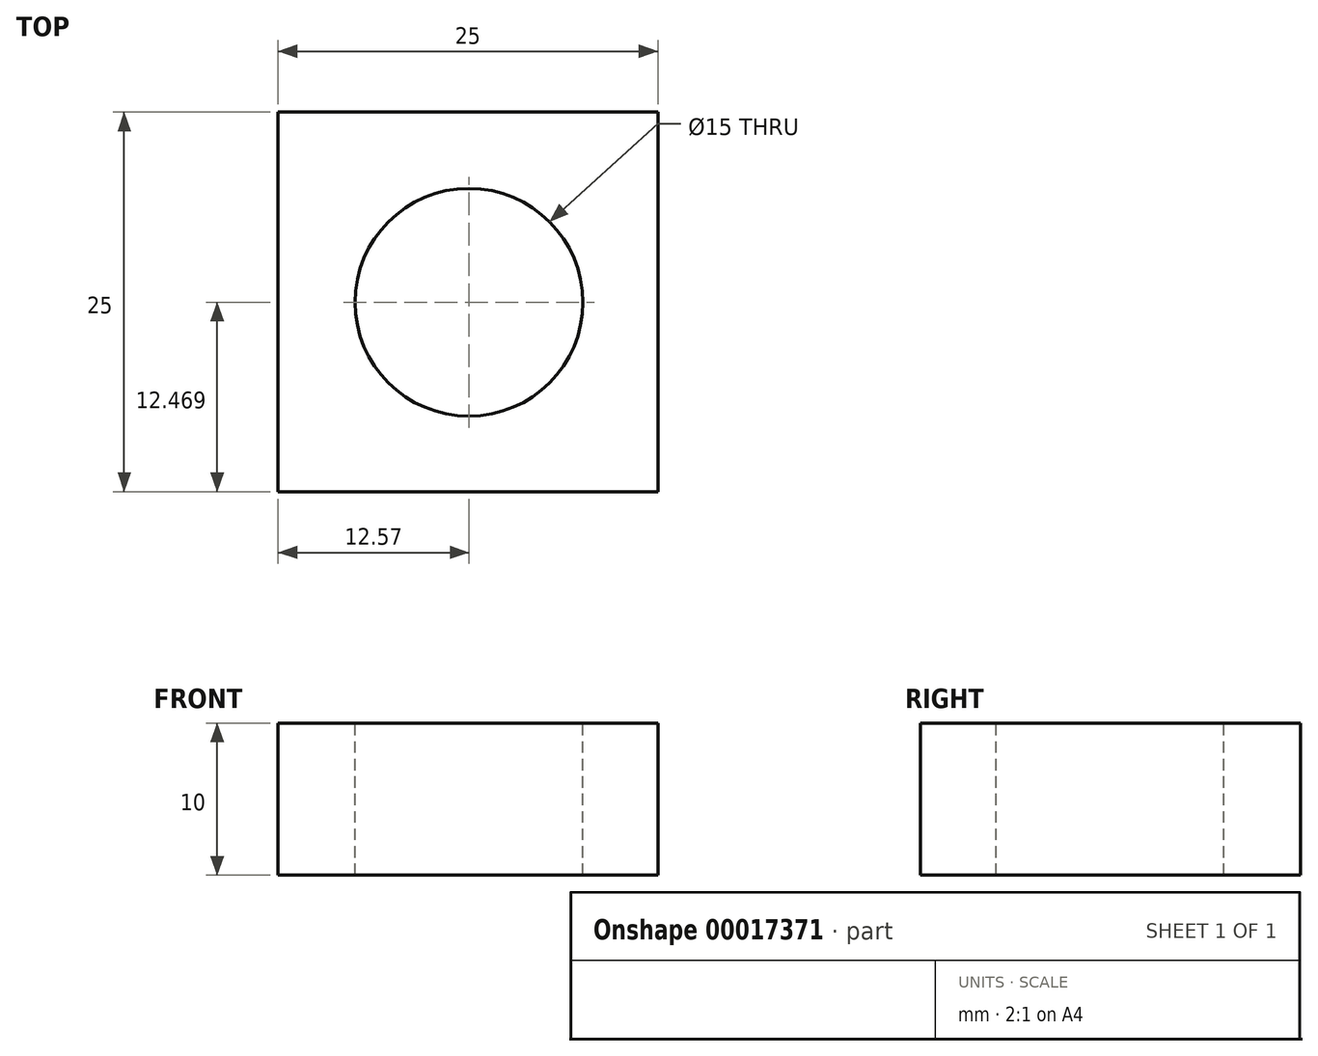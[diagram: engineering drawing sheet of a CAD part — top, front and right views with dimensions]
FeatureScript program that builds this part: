
annotation { "Feature Type Name" : "Feature", "Feature Type Description" : "" }
export const myFeature = defineFeature(function(context is Context, id is Id, definition is map)
    precondition{}
    {
        {
            var Q0;
            Q0=qCreatedBy(makeId("Front.planeOp"),FACE);
            var sketch = newSketch(context, id + "F0", { "sketchPlane" : qUnion([Q0])});
            skLineSegment(sketch, "E0", {"start": v(-21.22, 10) * mm, "end": v(-21.22, 0) * mm});
            skLineSegment(sketch, "E1", {"start": v(-21.22, 0) * mm, "end": v(3.78, 0) * mm});
            skLineSegment(sketch, "E2", {"start": v(3.78, 0) * mm, "end": v(3.78, 10) * mm});
            skLineSegment(sketch, "E3", {"start": v(3.78, 10) * mm, "end": v(-21.22, 10) * mm});
            skSolve(sketch);
        }
        {
            var Q0;
            Q0=makeQuery(id+"F0.imprint","IMPRINT",FACE,{"disambiguationData":[TD([[makeQuery(id+"F0.imprint","IMPRINT",EDGE,{"derivedFrom":sQuery(id+"F0.wireOp",EDGE,"E0")}),1.0]])]});
            extrude(context, id + "F1", {"entities" : qUnion([Q0]), "oppositeDirection" : true, "depth" : 25 * mm});
        }
        {
            var Q0;
            Q0=makeQuery(id+"F1.opExtrude","SWEPT_FACE",FACE,{"disambiguationData":[OSD([sQuery(id+"F0.wireOp",EDGE,"E3")])]});
            var sketch = newSketch(context, id + "F2", { "sketchPlane" : qUnion([Q0])});
            skCircle(sketch, "E4", {"center": v(-8.65, 12.47) * mm, "radius": 7.5 * mm});
            skSolve(sketch);
        }
        {
            var Q0;
            Q0=makeQuery(id+"F2.imprint","IMPRINT",FACE,{"disambiguationData":[TD([[makeQuery(id+"F2.imprint","IMPRINT",EDGE,{"derivedFrom":sQuery(id+"F2.wireOp",EDGE,"E4")}),1.0]])]});
            extrude(context, id + "F3", {"entities" : qUnion([Q0]), "operationType" : NewBodyOperationType.REMOVE, "oppositeDirection" : true, "depth" : 25 * mm});
        }
    });
